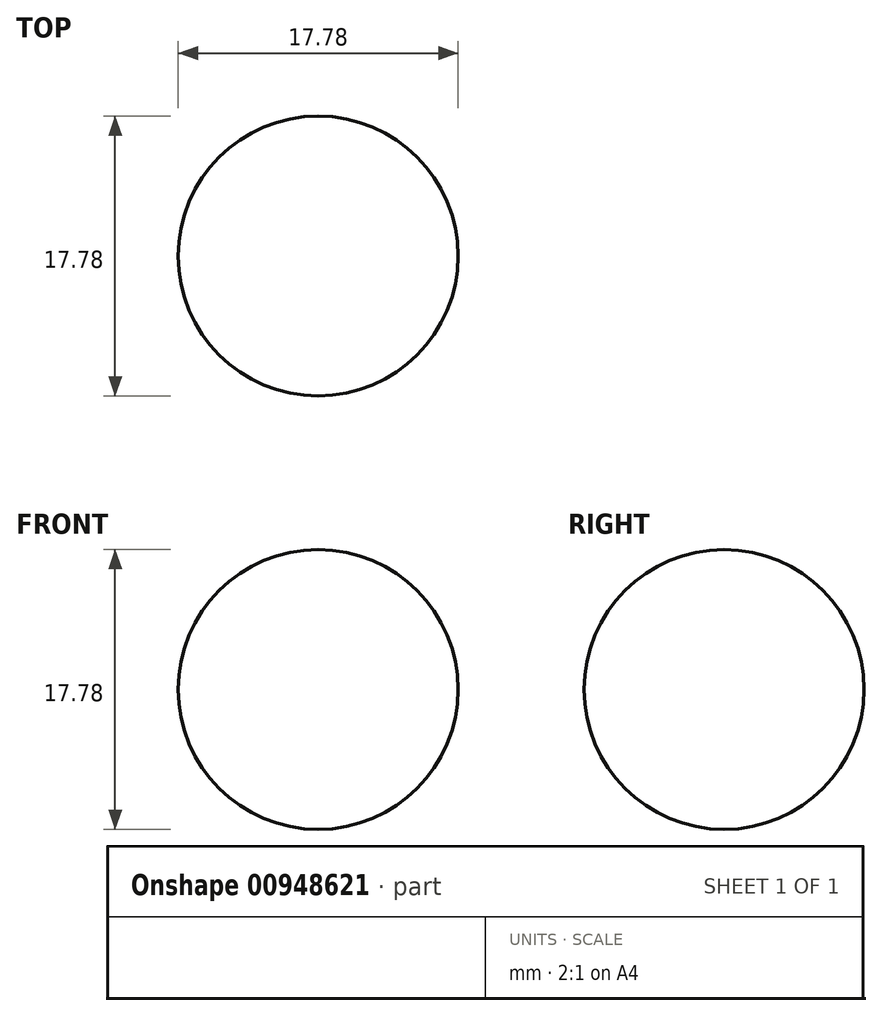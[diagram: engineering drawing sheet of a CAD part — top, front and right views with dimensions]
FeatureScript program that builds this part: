
annotation { "Feature Type Name" : "Feature", "Feature Type Description" : "" }
export const myFeature = defineFeature(function(context is Context, id is Id, definition is map)
    precondition{}
    {
        {
            var Q0;
            Q0=qCreatedBy(makeId("Top.planeOp"),FACE);
            var sketch = newSketch(context, id + "F0", { "sketchPlane" : qUnion([Q0])});
            skLineSegment(sketch, "E0", {"start": v(0, 0) * mm, "end": v(0, -17.78) * mm});
            skArc(sketch, "E1", {"start": v(0, -17.78) * mm, "mid": v(8.9, -8.9) * mm, "end": v(0, 0) * mm});
            skSolve(sketch);
        }
        {
            var Q0;
            Q0 = qSketchRegion(id + "F0", true);
            var Q1;
            Q1=sQuery(id+"F0.wireOp",EDGE,"E0");
            revolve(context, id + "F1", {"surfaceOperationType" : NewSurfaceOperationType.NEW, "entities" : qUnion([Q0]), "axis" : qUnion([Q1]), "revolveType" : RevolveType.FULL});
        }
    });
